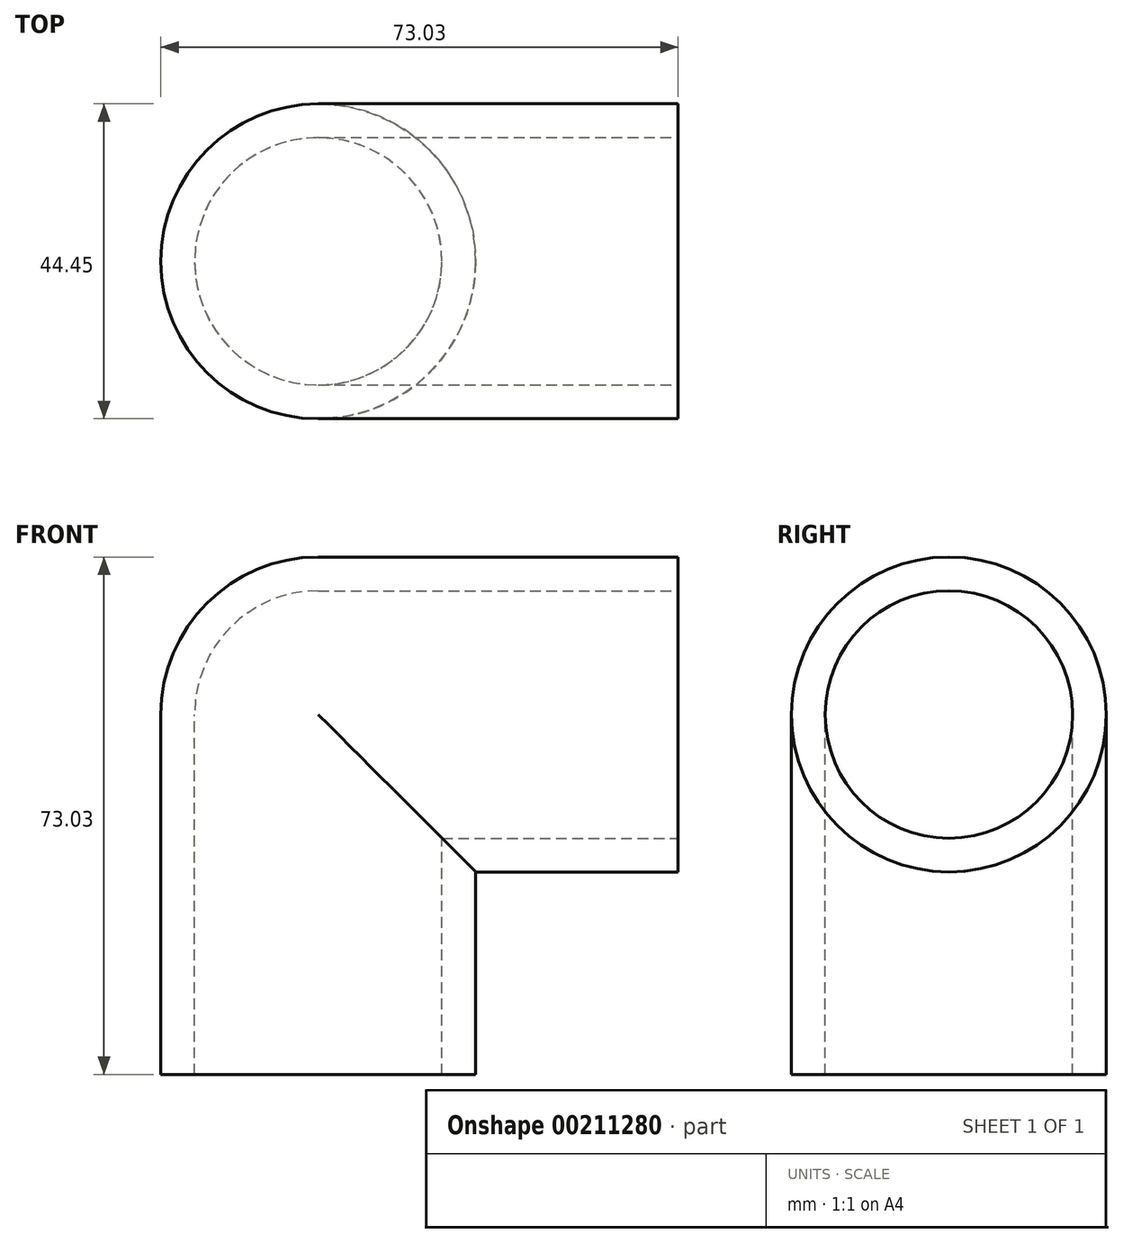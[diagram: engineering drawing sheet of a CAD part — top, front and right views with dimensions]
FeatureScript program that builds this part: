
annotation { "Feature Type Name" : "Feature", "Feature Type Description" : "" }
export const myFeature = defineFeature(function(context is Context, id is Id, definition is map)
    precondition{}
    {
        {
            var Q0;
            Q0=qCreatedBy(makeId("Front.planeOp"),FACE);
            var sketch = newSketch(context, id + "F0", { "sketchPlane" : qUnion([Q0])});
            skLineSegment(sketch, "E0", {"start": v(0, 0) * mm, "end": v(-22.23, 0) * mm});
            skLineSegment(sketch, "E1", {"start": v(-22.23, 0) * mm, "end": v(-22.23, -50.8) * mm});
            skLineSegment(sketch, "E2", {"start": v(0, 0) * mm, "end": v(50.8, 0) * mm});
            skLineSegment(sketch, "E3", {"start": v(50.8, 0) * mm, "end": v(50.8, 22.23) * mm});
            skLineSegment(sketch, "E4", {"start": v(50.8, 22.23) * mm, "end": v(-22.23, 22.23) * mm});
            skLineSegment(sketch, "E5", {"start": v(-22.23, 22.23) * mm, "end": v(-22.23, -50.8) * mm});
            skLineSegment(sketch, "E6", {"start": v(-22.23, -50.8) * mm, "end": v(22.23, -50.8) * mm});
            skLineSegment(sketch, "E7", {"start": v(22.23, -50.8) * mm, "end": v(22.23, -22.22) * mm});
            skLineSegment(sketch, "E8", {"start": v(22.23, -22.22) * mm, "end": v(50.8, -22.22) * mm});
            skLineSegment(sketch, "E9", {"start": v(50.8, -22.22) * mm, "end": v(50.8, 0) * mm});
            skSolve(sketch);
        }
        {
            var Q0;
            Q0 = qSketchRegion(id + "F0", true);
            extrude(context, id + "F1", {"entities" : qUnion([Q0]), "depth" : 44.45 * mm});
        }
        {
            var Q0;
            Q0=makeQuery(id+"F1.opExtrude","SWEPT_EDGE",EDGE,{"disambiguationData":[OSD([sQuery(id+"F0.wireOp",EDGE,"E4"),sQuery(id+"F0.wireOp",EDGE,"E5")])]});
            var Q1;
            Q1=makeQuery(id+"F1.opExtrude","CAP_EDGE",EDGE,{"disambiguationData":[OSD([sQuery(id+"F0.wireOp",EDGE,"E5")])],"isStart":false});
            var Q2;
            Q2=makeQuery(id+"F1.opExtrude","CAP_EDGE",EDGE,{"disambiguationData":[OSD([sQuery(id+"F0.wireOp",EDGE,"E4")])],"isStart":false});
            var Q3;
            Q3=makeQuery(id+"F1.opExtrude","CAP_EDGE",EDGE,{"disambiguationData":[OSD([sQuery(id+"F0.wireOp",EDGE,"E5")])],"isStart":true});
            var Q4;
            Q4=makeQuery(id+"F1.opExtrude","CAP_EDGE",EDGE,{"disambiguationData":[OSD([sQuery(id+"F0.wireOp",EDGE,"E4")])],"isStart":true});
            var Q5;
            Q5=makeQuery(id+"F1.opExtrude","CAP_EDGE",EDGE,{"disambiguationData":[OSD([sQuery(id+"F0.wireOp",EDGE,"E7")])],"isStart":false});
            var Q6;
            Q6=makeQuery(id+"F1.opExtrude","CAP_EDGE",EDGE,{"disambiguationData":[OSD([sQuery(id+"F0.wireOp",EDGE,"E8")])],"isStart":false});
            var Q7;
            Q7=makeQuery(id+"F1.opExtrude","CAP_EDGE",EDGE,{"disambiguationData":[OSD([sQuery(id+"F0.wireOp",EDGE,"E8")])],"isStart":true});
            var Q8;
            Q8=makeQuery(id+"F1.opExtrude","CAP_EDGE",EDGE,{"disambiguationData":[OSD([sQuery(id+"F0.wireOp",EDGE,"E7")])],"isStart":true});
            fillet(context, id + "F2", {"entities" : qUnion([Q0, Q1, Q2, Q3, Q4, Q5, Q6, Q7, Q8]), "radius" : 22.22 * mm, "tangentPropagation" : true, "allowEdgeOverflow" : false});
        }
        {
            var Q0;
            Q0=makeQuery(id+"F1.opExtrude","SWEPT_FACE",FACE,{"disambiguationData":[OSD([sQuery(id+"F0.wireOp",EDGE,"E6")])]});
            var Q1;
            Q1=makeQuery(id+"F1.opExtrude","SWEPT_FACE",FACE,{"disambiguationData":[OSD([sQuery(id+"F0.wireOp",EDGE,"E3"),sQuery(id+"F0.wireOp",EDGE,"E9")])]});
            shell(context, id + "F3", {"entities" : qUnion([Q0, Q1]), "thickness" : 4.76 * mm});
        }
    });
